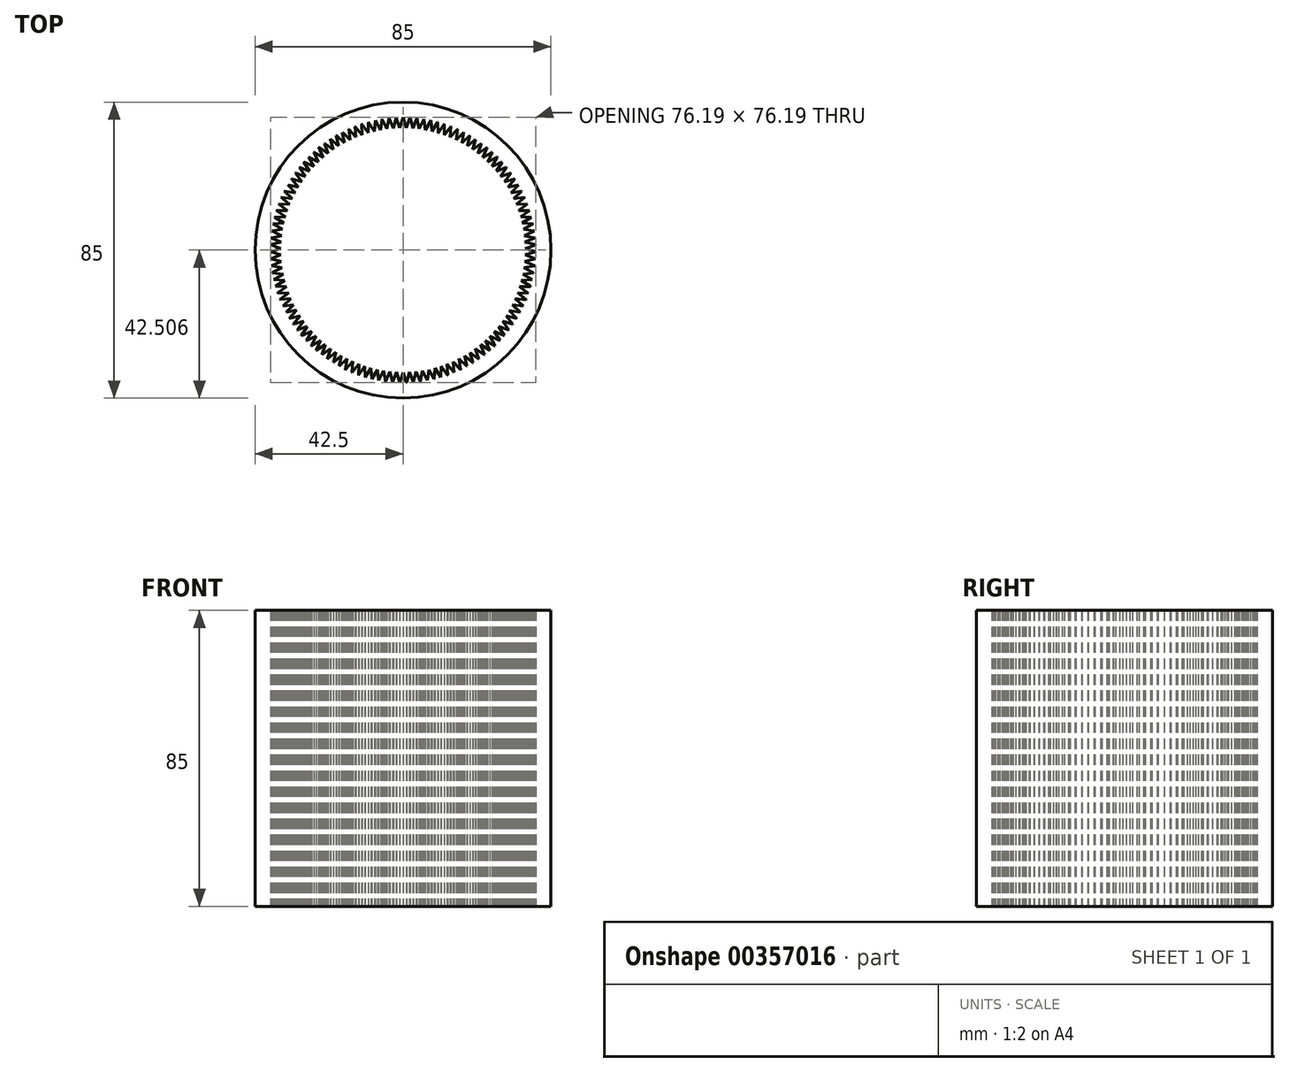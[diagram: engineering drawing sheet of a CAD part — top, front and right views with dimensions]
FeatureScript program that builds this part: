
annotation { "Feature Type Name" : "Feature", "Feature Type Description" : "" }
export const myFeature = defineFeature(function(context is Context, id is Id, definition is map)
    precondition{}
    {
        {
            var Q0;
            Q0=qCreatedBy(makeId("Top.planeOp"),FACE);
            var sketch = newSketch(context, id + "F0", { "sketchPlane" : qUnion([Q0])});
            skCircle(sketch, "E0", {"center": v(0, 0) * mm, "radius": 38.1 * mm});
            skCircle(sketch, "E1", {"center": v(0, 0) * mm, "radius": 42.5 * mm});
            skLineSegment(sketch, "E2", {"start": v(0, 0) * mm, "end": v(0, 59.15) * mm, "construction": true});
            skLineSegment(sketch, "E3", {"start": v(0, 0) * mm, "end": v(-3.13, 59.79) * mm, "construction": true});
            skLineSegment(sketch, "E4", {"start": v(0, 38.1) * mm, "end": v(0, 35.1) * mm});
            skLineSegment(sketch, "E5", {"start": v(0, 35.1) * mm, "end": v(-1.84, 35.1) * mm, "construction": true});
            skLineSegment(sketch, "E6", {"start": v(-1.84, 35.1) * mm, "end": v(-2, 38.05) * mm});
            skLineSegment(sketch, "E7", {"start": v(-2, 38.05) * mm, "end": v(-0.92, 35.1) * mm});
            skLineSegment(sketch, "E8", {"start": v(-0.92, 35.1) * mm, "end": v(0, 38.1) * mm});
            skSolve(sketch);
        }
        {
            var Q0;
            Q0=makeQuery(id+"F0.imprint","IMPRINT",FACE,{"disambiguationData":[TD([[makeQuery(id+"F0.imprint","IMPRINT",EDGE,{"derivedFrom":sQuery(id+"F0.wireOp",EDGE,"E1")}),1.0]])]});
            var Q1;
            {var subQ2=sQuery(id+"F0.wireOp",EDGE,"E7");Q1=makeQuery(id+"F0.imprint","IMPRINT",FACE,{"disambiguationData":[TD([[makeQuery(id+"F0.imprint","IMPRINT",EDGE,{"derivedFrom":subQ2}),1.0]])]});}
            extrude(context, id + "F1", {"entities" : qUnion([Q0, Q1]), "depth" : 10 * mm});
        }
        {
            var Q0;
            Q0=makeQuery(id+"F1.opExtrude","SWEPT_FACE",FACE,{"disambiguationData":[OSD([sQuery(id+"F0.wireOp",EDGE,"E7")])]});
            var Q1;
            Q1=makeQuery(id+"F1.opExtrude","SWEPT_FACE",FACE,{"disambiguationData":[OSD([sQuery(id+"F0.wireOp",EDGE,"E8")])]});
            var Q2;
            Q2=makeQuery(id+"F1.opExtrude","SWEPT_FACE",FACE,{"disambiguationData":[OSD([sQuery(id+"F0.wireOp",EDGE,"E0")])]});
            circularPattern(context, id + "F2", {"patternType" : PatternType.FACE, "faces" : qUnion([Q0, Q1]), "axis" : qUnion([Q2]), "angle" : 360 * degree, "instanceCount" : 119, "equalSpace" : true});
        }
        {
            var Q0;
            Q0=makeQuery(id+"F1.opExtrude","CAP_FACE",FACE,{"disambiguationData":[OSD([sQuery(id+"F0.wireOp",EDGE,"E0"),sQuery(id+"F0.wireOp",EDGE,"E1"),sQuery(id+"F0.wireOp",EDGE,"E7"),sQuery(id+"F0.wireOp",EDGE,"E8")])],"isStart":false});
            var Q1;
            Q1=makeQuery(id+"F1.opExtrude","CAP_FACE",FACE,{"disambiguationData":[OSD([sQuery(id+"F0.wireOp",EDGE,"E0"),sQuery(id+"F0.wireOp",EDGE,"E1"),sQuery(id+"F0.wireOp",EDGE,"E7"),sQuery(id+"F0.wireOp",EDGE,"E8")])],"isStart":true});
            extrude(context, id + "F3", {"entities" : qUnion([Q0, Q1]), "operationType" : NewBodyOperationType.ADD, "depth" : 25 * mm});
        }
        {
            var Q0;
            {var subQ0=sQuery(id+"F0.wireOp",EDGE,"E8");var subQ1=sQuery(id+"F0.wireOp",EDGE,"E7");var subQ2=sQuery(id+"F0.wireOp",EDGE,"E1");var subQ3=sQuery(id+"F0.wireOp",EDGE,"E0");Q0=makeQuery(id+"F3.opExtrude","CAP_FACE",FACE,{"disambiguationData":[OSD([subQ3,subQ2,subQ1,subQ0]),TDD([makeQuery(id+"F1.opExtrude","CAP_FACE",FACE,{"disambiguationData":[OSD([subQ3,subQ2,subQ1,subQ0])],"isStart":false})])],"isStart":false});}
            extrude(context, id + "F4", {"entities" : qUnion([Q0]), "operationType" : NewBodyOperationType.ADD, "depth" : 50 * mm});
        }
    });
